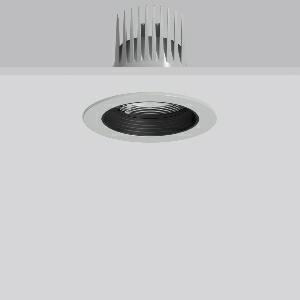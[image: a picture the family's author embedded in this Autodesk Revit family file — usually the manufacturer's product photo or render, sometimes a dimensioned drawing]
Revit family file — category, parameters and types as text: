
# Revit family: heledon_maxi_e_901769_004_76_98b0
name_source: partatom
category: Lighting Fixtures
units: mm (PartAtom-declared; Revit-internal decimal feet)

## family parameters
Cut with Voids When Loaded = No
Host = Face
Light Source = No
Part Type = Normal
Room Calculation Point = No
Round Connector Dimension = Use Diameter
Shared = No

## types (1)
- HELEDON maxi E (1 x LED Modul 930, 3600 lm, 3000)
    Apparent Load = 35 VA
    Approval mark = CE
    CIE Flux Codes = 96 100 100 100 100
    Color Rendering = 90
    Color Temperature = 3000
    Default Elevation = 1800 mm
    Description = Series: HELEDON maxi
Round recessed downlight. Housing: die-cast aluminium, powder-coated. Black plastic ring and recessed LED to prevent glare from the side. Optical assembly with lens made of plastic (polycarbonate) for the best homogeneous light distribution - can be changed without tools. Best colour rendering index Ra>90. Suitable for Recessed ceiling mounting. Installation without tools thanks to spring fastening system. Including separate LED converter with connecting cable 600 mm.High quality converter without flickering and stroboscopic effect. Through-wiring box (5 pole) available as accessory. The following accessories can be mounted without use of tools: interchangeable lenses, decorative glasses, honeycomb louvre, clear and frosted diffusers, white interchangeable plastic ring. 
Colour: silver
Diameter: 162 mm
Height: 3 mm
Cut-out diameter: 152 mm
Recess height: 200 mm
Luminaire: recess height: 135 mm
Lamp: LED
Socket: without socket
Colour temperature: 3000K
Colour rendering index (CRI): 92
System power: 35 W
Rated luminous flux: 3600 lm
Luminous efficiency: 103 lm/W
Control gear: Converter, dimmable, DALI
Protection class: II
Type of protection: IP 20
    Height = 0 mm  [stored 0 ft]
    Lamp = 1 x LED Modul 930
    Lamp Light Flux = 3600 lm
    Lamp count = 1
    Length = 162 mm
    Lifetime = 50000 h
    Luminous efficacy = 103 lm/W
    Manufacturer = RZB
    ModVariant = No
    Model = 901769.004.76
    Mounting Place = Ceiling
    Mounting Type = Recessed
    Number of Poles = 1
    OnlyDefault = Yes
    Power Factor = 1
    Product Name = HELEDON maxi E
    Product group = Recessed downlights
    ProductGroupID = 402
    Protection Class = Protection class II
    Protection Degree = IP 20
    RLX_Detail_Level = 1
    RLX_Emergency_Light_Flux = 0 lm
    RLX_Emergency_Type = 0
    RLX_Emergency_Type_DB = No
    RlxData = <blob elided: 120281 chars, md5=85c96584>
    Socket = socket
    Standby Power = 0 W
    System Light Flux = 3600 lm
    System Power = 35 W
    Type Comments = Product without accessories
    Type Image = 901663.004.jpg
    URL = http://relux.com
    VarID = ---
    Voltage = 230 V
    Voltage Range = 220-240 V
    Weight = 0.00 kg
    Width = 0 mm  [stored 0 ft]

note: [stored X ft] marks values corroborated as IEEE doubles in the binary element streams (Revit-internal decimal feet)

## geometry (parser evidence)
native form markers: Blend x4, Sweep x11
no freeform markers — native parametric forms only
